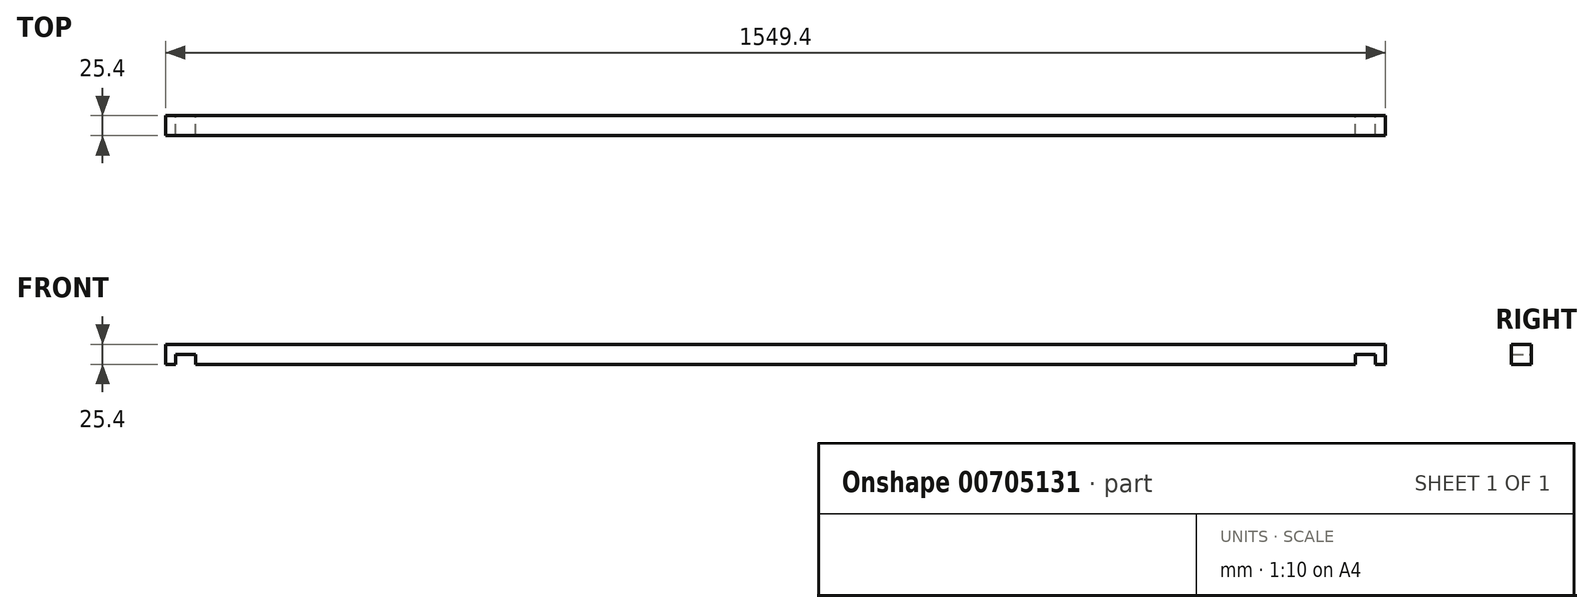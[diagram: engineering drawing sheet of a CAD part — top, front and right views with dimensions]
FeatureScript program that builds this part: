
annotation { "Feature Type Name" : "Feature", "Feature Type Description" : "" }
export const myFeature = defineFeature(function(context is Context, id is Id, definition is map)
    precondition{}
    {
        {
            var Q0;
            Q0=qCreatedBy(makeId("Front.planeOp"),FACE);
            var sketch = newSketch(context, id + "F0", { "sketchPlane" : qUnion([Q0])});
            skLineSegment(sketch, "E0.bottom", {"start": v(774.7, -12.7) * mm, "end": v(762, -12.7) * mm});
            skLineSegment(sketch, "E0.top", {"start": v(774.7, 12.7) * mm, "end": v(-774.7, 12.7) * mm});
            skLineSegment(sketch, "E0.left", {"start": v(774.7, -12.7) * mm, "end": v(774.7, 12.7) * mm});
            skLineSegment(sketch, "E0.right", {"start": v(-774.7, -12.7) * mm, "end": v(-774.7, 12.7) * mm});
            skPoint(sketch, "E0.middle", {"position": v(0, 0) * mm});
            skLineSegment(sketch, "E1.top", {"start": v(-762, 0) * mm, "end": v(-736.6, 0) * mm});
            skLineSegment(sketch, "E1.left", {"start": v(-762, -12.7) * mm, "end": v(-762, 0) * mm});
            skLineSegment(sketch, "E1.right", {"start": v(-736.6, -12.7) * mm, "end": v(-736.6, 0) * mm});
            skLineSegment(sketch, "E2.top", {"start": v(762, 0) * mm, "end": v(736.6, 0) * mm});
            skLineSegment(sketch, "E2.left", {"start": v(762, -12.7) * mm, "end": v(762, 0) * mm});
            skLineSegment(sketch, "E2.right", {"start": v(736.6, -12.7) * mm, "end": v(736.6, 0) * mm});
            skLineSegment(sketch, "E3.trimOffspring", {"start": v(736.6, -12.7) * mm, "end": v(-736.6, -12.7) * mm});
            skLineSegment(sketch, "E4.trimOffspring", {"start": v(-762, -12.7) * mm, "end": v(-774.7, -12.7) * mm});
            skSolve(sketch);
        }
        {
            var Q0;
            Q0 = qSketchRegion(id + "F0", true);
            extrude(context, id + "F1", {"entities" : qUnion([Q0]), "depth" : 25.4 * mm, "offsetDistance" : 25.4 * mm});
        }
    });
